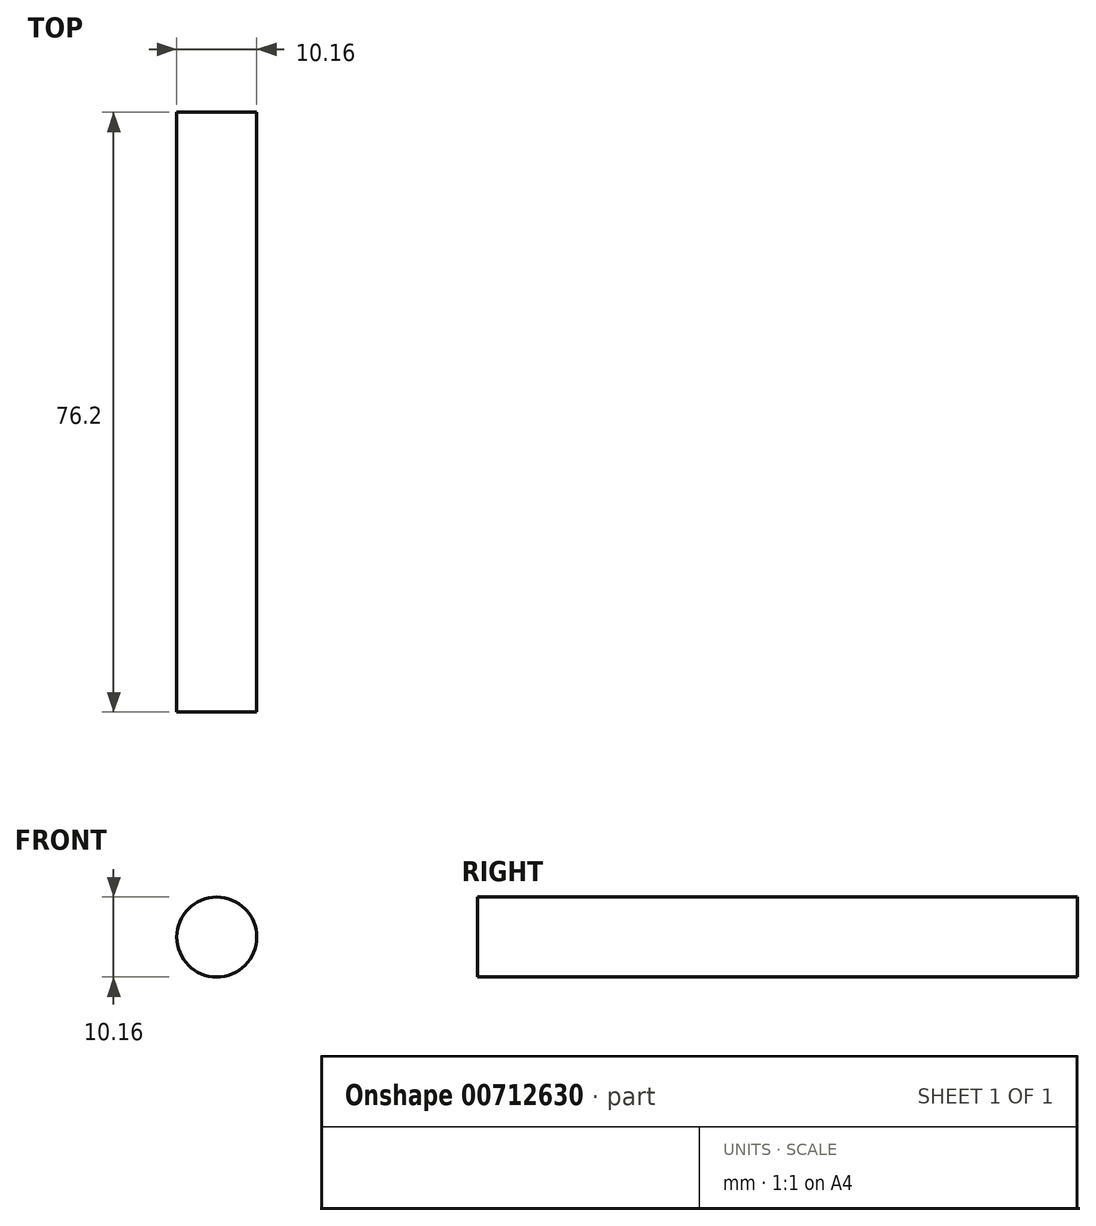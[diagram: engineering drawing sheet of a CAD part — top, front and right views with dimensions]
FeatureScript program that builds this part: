
annotation { "Feature Type Name" : "Feature", "Feature Type Description" : "" }
export const myFeature = defineFeature(function(context is Context, id is Id, definition is map)
    precondition{}
    {
        {
            var Q0;
            Q0=qCreatedBy(makeId("Front.planeOp"),FACE);
            var sketch = newSketch(context, id + "F0", { "sketchPlane" : qUnion([Q0])});
            skCircle(sketch, "E0", {"center": v(0, 0) * mm, "radius": 5.08 * mm});
            skSolve(sketch);
        }
        {
            var Q0;
            Q0=makeQuery(id+"F0.imprint","IMPRINT",FACE,{"disambiguationData":[TD([[makeQuery(id+"F0.imprint","IMPRINT",EDGE,{"derivedFrom":sQuery(id+"F0.wireOp",EDGE,"E0")}),1.0]])]});
            extrude(context, id + "F1", {"entities" : qUnion([Q0]), "endBound" : BoundingType.SYMMETRIC, "depth" : 76.2 * mm, "offsetDistance" : 25.4 * mm});
        }
    });
